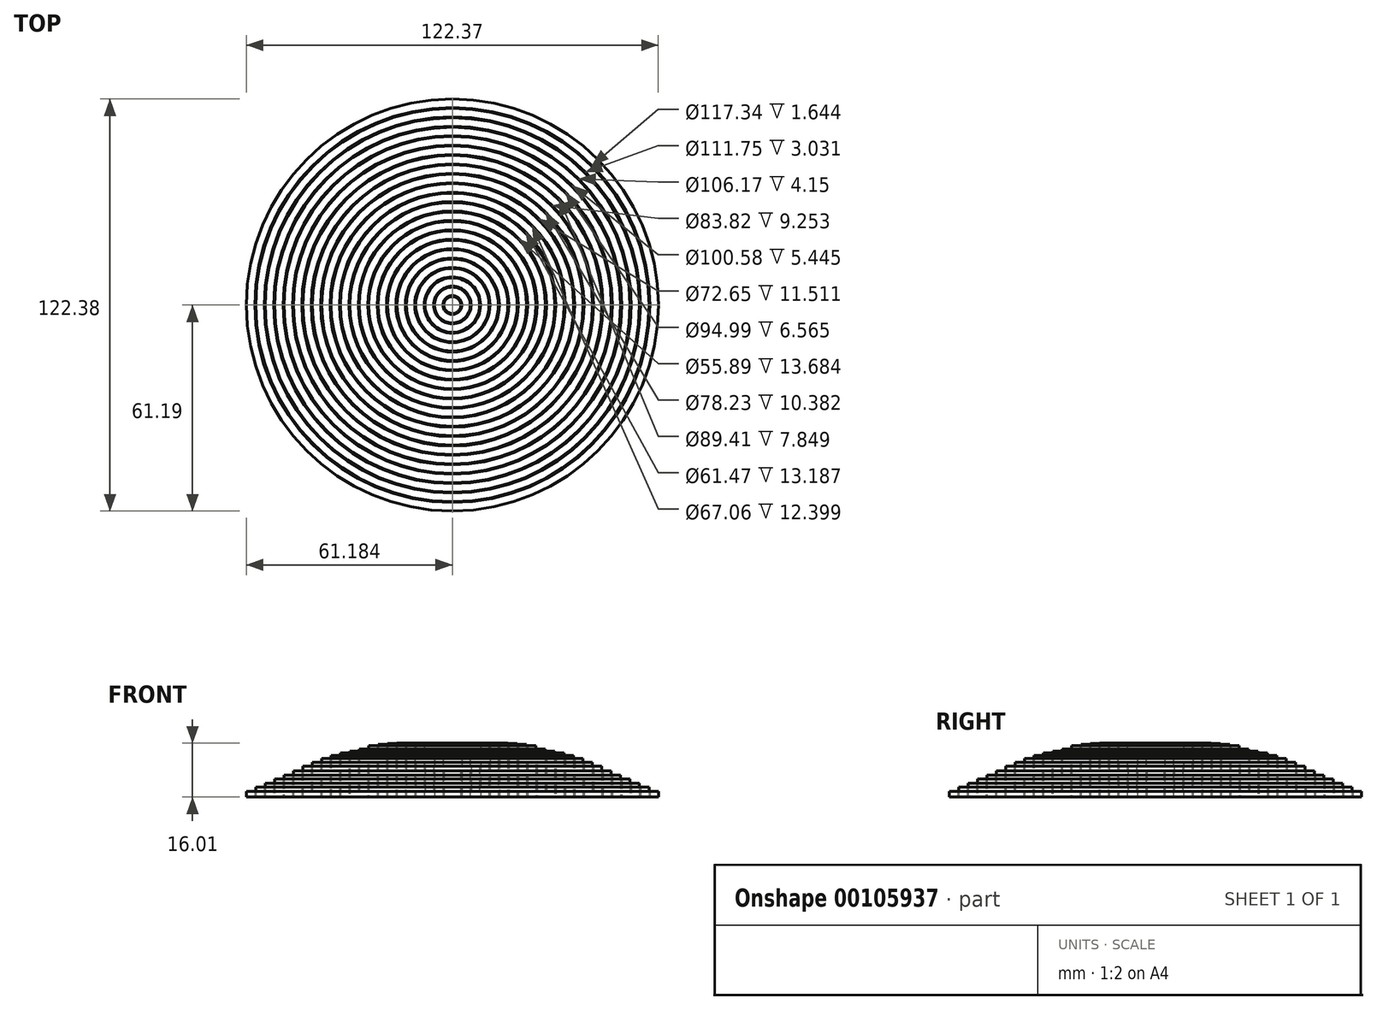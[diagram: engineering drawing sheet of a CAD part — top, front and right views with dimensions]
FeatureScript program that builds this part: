
annotation { "Feature Type Name" : "Feature", "Feature Type Description" : "" }
export const myFeature = defineFeature(function(context is Context, id is Id, definition is map)
    precondition{}
    {
        {
            var Q0;
            Q0=qCreatedBy(makeId("Front.planeOp"),FACE);
            var sketch = newSketch(context, id + "F0", { "sketchPlane" : qUnion([Q0])});
            skLineSegment(sketch, "E0", {"start": v(0, 7.88) * mm, "end": v(2.51, 7.88) * mm});
            skLineSegment(sketch, "E1", {"start": v(2.51, 7.88) * mm, "end": v(2.51, 0.01) * mm});
            skLineSegment(sketch, "E2", {"start": v(2.51, 0.01) * mm, "end": v(0, 0.01) * mm});
            skLineSegment(sketch, "E3", {"start": v(0, 0.01) * mm, "end": v(0, 7.88) * mm});
            skLineSegment(sketch, "E4", {"start": v(2.8, 11.92) * mm, "end": v(5.3, 11.92) * mm});
            skLineSegment(sketch, "E5", {"start": v(5.3, 11.92) * mm, "end": v(5.3, 0.01) * mm});
            skLineSegment(sketch, "E6", {"start": v(5.3, 0.01) * mm, "end": v(2.8, 0.01) * mm});
            skLineSegment(sketch, "E7", {"start": v(2.8, 0.01) * mm, "end": v(2.8, 11.92) * mm});
            skLineSegment(sketch, "E8", {"start": v(5.6, 14.05) * mm, "end": v(8.1, 14.05) * mm});
            skLineSegment(sketch, "E9", {"start": v(8.1, 14.05) * mm, "end": v(8.1, 0.01) * mm});
            skLineSegment(sketch, "E10", {"start": v(8.1, 0.01) * mm, "end": v(5.6, 0.01) * mm});
            skLineSegment(sketch, "E11", {"start": v(5.6, 0.01) * mm, "end": v(5.6, 14.05) * mm});
            skLineSegment(sketch, "E12", {"start": v(8.39, 15.15) * mm, "end": v(10.9, 15.15) * mm});
            skLineSegment(sketch, "E13", {"start": v(10.9, 15.15) * mm, "end": v(10.9, 0.01) * mm});
            skLineSegment(sketch, "E14", {"start": v(10.9, 0.01) * mm, "end": v(8.39, 0.01) * mm});
            skLineSegment(sketch, "E15", {"start": v(8.39, 0.01) * mm, "end": v(8.39, 15.15) * mm});
            skLineSegment(sketch, "E16", {"start": v(11.18, 15.76) * mm, "end": v(13.69, 15.76) * mm});
            skLineSegment(sketch, "E17", {"start": v(13.69, 15.76) * mm, "end": v(13.69, 0.01) * mm});
            skLineSegment(sketch, "E18", {"start": v(13.69, 0.01) * mm, "end": v(11.18, 0.01) * mm});
            skLineSegment(sketch, "E19", {"start": v(11.18, 0.01) * mm, "end": v(11.18, 15.76) * mm});
            skLineSegment(sketch, "E20", {"start": v(13.98, 16.02) * mm, "end": v(16.48, 16.02) * mm});
            skLineSegment(sketch, "E21", {"start": v(16.48, 16.02) * mm, "end": v(16.48, 0.01) * mm});
            skLineSegment(sketch, "E22", {"start": v(16.48, 0.01) * mm, "end": v(13.98, 0.01) * mm});
            skLineSegment(sketch, "E23", {"start": v(13.98, 0.01) * mm, "end": v(13.98, 16.02) * mm});
            skLineSegment(sketch, "E24", {"start": v(16.77, 16) * mm, "end": v(19.27, 16) * mm});
            skLineSegment(sketch, "E25", {"start": v(19.27, 16) * mm, "end": v(19.27, 0.01) * mm});
            skLineSegment(sketch, "E26", {"start": v(19.27, 0.01) * mm, "end": v(16.77, 0.01) * mm});
            skLineSegment(sketch, "E27", {"start": v(16.77, 0.01) * mm, "end": v(16.77, 16) * mm});
            skLineSegment(sketch, "E28", {"start": v(19.57, 15.64) * mm, "end": v(22.07, 15.64) * mm});
            skLineSegment(sketch, "E29", {"start": v(22.07, 15.64) * mm, "end": v(22.07, 0.01) * mm});
            skLineSegment(sketch, "E30", {"start": v(22.07, 0.01) * mm, "end": v(19.57, 0.01) * mm});
            skLineSegment(sketch, "E31", {"start": v(19.57, 0.01) * mm, "end": v(19.57, 15.64) * mm});
            skLineSegment(sketch, "E32", {"start": v(22.36, 15.26) * mm, "end": v(24.86, 15.26) * mm});
            skLineSegment(sketch, "E33", {"start": v(24.86, 15.26) * mm, "end": v(24.86, 0.01) * mm});
            skLineSegment(sketch, "E34", {"start": v(24.86, 0.01) * mm, "end": v(22.36, 0.01) * mm});
            skLineSegment(sketch, "E35", {"start": v(22.36, 0.01) * mm, "end": v(22.36, 15.26) * mm});
            skLineSegment(sketch, "E36", {"start": v(25.15, 14.32) * mm, "end": v(27.66, 14.32) * mm});
            skLineSegment(sketch, "E37", {"start": v(27.66, 14.32) * mm, "end": v(27.66, 0.01) * mm});
            skLineSegment(sketch, "E38", {"start": v(27.66, 0.01) * mm, "end": v(25.15, 0.01) * mm});
            skLineSegment(sketch, "E39", {"start": v(25.15, 0.01) * mm, "end": v(25.15, 14.32) * mm});
            skLineSegment(sketch, "E40", {"start": v(27.95, 13.7) * mm, "end": v(30.45, 13.7) * mm});
            skLineSegment(sketch, "E41", {"start": v(30.45, 13.7) * mm, "end": v(30.45, 0.01) * mm});
            skLineSegment(sketch, "E42", {"start": v(30.45, 0.01) * mm, "end": v(27.95, 0.01) * mm});
            skLineSegment(sketch, "E43", {"start": v(27.95, 0.01) * mm, "end": v(27.95, 13.7) * mm});
            skLineSegment(sketch, "E44", {"start": v(30.74, 13.2) * mm, "end": v(33.24, 13.2) * mm});
            skLineSegment(sketch, "E45", {"start": v(33.24, 13.2) * mm, "end": v(33.24, 0.01) * mm});
            skLineSegment(sketch, "E46", {"start": v(33.24, 0.01) * mm, "end": v(30.74, 0.01) * mm});
            skLineSegment(sketch, "E47", {"start": v(30.74, 0.01) * mm, "end": v(30.74, 13.2) * mm});
            skLineSegment(sketch, "E48", {"start": v(33.53, 12.41) * mm, "end": v(36.04, 12.41) * mm});
            skLineSegment(sketch, "E49", {"start": v(36.04, 12.41) * mm, "end": v(36.04, 0.01) * mm});
            skLineSegment(sketch, "E50", {"start": v(36.04, 0.01) * mm, "end": v(33.53, 0.01) * mm});
            skLineSegment(sketch, "E51", {"start": v(33.53, 0.01) * mm, "end": v(33.53, 12.41) * mm});
            skLineSegment(sketch, "E52", {"start": v(36.33, 11.52) * mm, "end": v(38.83, 11.52) * mm});
            skLineSegment(sketch, "E53", {"start": v(38.83, 11.52) * mm, "end": v(38.83, 0.01) * mm});
            skLineSegment(sketch, "E54", {"start": v(38.83, 0.01) * mm, "end": v(36.33, 0.01) * mm});
            skLineSegment(sketch, "E55", {"start": v(36.33, 0.01) * mm, "end": v(36.33, 11.52) * mm});
            skLineSegment(sketch, "E56", {"start": v(39.12, 10.4) * mm, "end": v(41.63, 10.4) * mm});
            skLineSegment(sketch, "E57", {"start": v(41.63, 10.4) * mm, "end": v(41.63, 0.01) * mm});
            skLineSegment(sketch, "E58", {"start": v(41.63, 0.01) * mm, "end": v(39.12, 0.01) * mm});
            skLineSegment(sketch, "E59", {"start": v(39.12, 0.01) * mm, "end": v(39.12, 10.4) * mm});
            skLineSegment(sketch, "E60", {"start": v(41.91, 9.27) * mm, "end": v(44.42, 9.27) * mm});
            skLineSegment(sketch, "E61", {"start": v(44.42, 9.27) * mm, "end": v(44.42, 0.01) * mm});
            skLineSegment(sketch, "E62", {"start": v(44.42, 0.01) * mm, "end": v(41.91, 0.01) * mm});
            skLineSegment(sketch, "E63", {"start": v(41.91, 0.01) * mm, "end": v(41.91, 9.27) * mm});
            skLineSegment(sketch, "E64", {"start": v(44.7, 7.86) * mm, "end": v(47.22, 7.86) * mm});
            skLineSegment(sketch, "E65", {"start": v(47.22, 7.86) * mm, "end": v(47.22, 0.01) * mm});
            skLineSegment(sketch, "E66", {"start": v(47.22, 0.01) * mm, "end": v(44.7, 0.01) * mm});
            skLineSegment(sketch, "E67", {"start": v(44.7, 0.01) * mm, "end": v(44.7, 7.86) * mm});
            skLineSegment(sketch, "E68", {"start": v(47.5, 6.58) * mm, "end": v(50.01, 6.58) * mm});
            skLineSegment(sketch, "E69", {"start": v(50.01, 6.58) * mm, "end": v(50.01, 0.01) * mm});
            skLineSegment(sketch, "E70", {"start": v(50.01, 0.01) * mm, "end": v(47.5, 0.01) * mm});
            skLineSegment(sketch, "E71", {"start": v(47.5, 0.01) * mm, "end": v(47.5, 6.58) * mm});
            skLineSegment(sketch, "E72", {"start": v(50.3, 5.46) * mm, "end": v(52.8, 5.46) * mm});
            skLineSegment(sketch, "E73", {"start": v(52.8, 5.46) * mm, "end": v(52.8, 0.01) * mm});
            skLineSegment(sketch, "E74", {"start": v(52.8, 0.01) * mm, "end": v(50.3, 0.01) * mm});
            skLineSegment(sketch, "E75", {"start": v(50.3, 0.01) * mm, "end": v(50.3, 5.46) * mm});
            skLineSegment(sketch, "E76", {"start": v(53.09, 4.16) * mm, "end": v(55.6, 4.16) * mm});
            skLineSegment(sketch, "E77", {"start": v(55.6, 4.16) * mm, "end": v(55.6, 0.01) * mm});
            skLineSegment(sketch, "E78", {"start": v(55.6, 0.01) * mm, "end": v(53.09, 0.01) * mm});
            skLineSegment(sketch, "E79", {"start": v(53.09, 0.01) * mm, "end": v(53.09, 4.16) * mm});
            skLineSegment(sketch, "E80", {"start": v(55.88, 3.04) * mm, "end": v(58.4, 3.04) * mm});
            skLineSegment(sketch, "E81", {"start": v(58.4, 3.04) * mm, "end": v(58.4, 0.01) * mm});
            skLineSegment(sketch, "E82", {"start": v(58.4, 0.01) * mm, "end": v(55.88, 0.01) * mm});
            skLineSegment(sketch, "E83", {"start": v(55.88, 0.01) * mm, "end": v(55.88, 3.04) * mm});
            skLineSegment(sketch, "E84", {"start": v(58.67, 1.66) * mm, "end": v(61.2, 1.66) * mm});
            skLineSegment(sketch, "E85", {"start": v(61.2, 1.66) * mm, "end": v(61.2, 0.01) * mm});
            skLineSegment(sketch, "E86", {"start": v(61.2, 0.01) * mm, "end": v(58.67, 0.01) * mm});
            skLineSegment(sketch, "E87", {"start": v(58.67, 0.01) * mm, "end": v(58.67, 1.66) * mm});
            skLineSegment(sketch, "E88", {"start": v(0, 0.01) * mm, "end": v(0, 29.32) * mm});
            skSolve(sketch);
        }
        {
            var Q0;
            {var subQ0=sQuery(id+"F0.wireOp",EDGE,"E0");Q0=makeQuery(id+"F0.imprint","IMPRINT",FACE,{"disambiguationData":[TD([[makeQuery(id+"F0.imprint","IMPRINT",EDGE,{"derivedFrom":subQ0}),-1.0]])]});}
            var Q1;
            Q1=makeQuery(id+"F0.imprint","IMPRINT",FACE,{"disambiguationData":[TD([[makeQuery(id+"F0.imprint","IMPRINT",EDGE,{"derivedFrom":sQuery(id+"F0.wireOp",EDGE,"E4")}),-1.0]])]});
            var Q2;
            Q2=makeQuery(id+"F0.imprint","IMPRINT",FACE,{"disambiguationData":[TD([[makeQuery(id+"F0.imprint","IMPRINT",EDGE,{"derivedFrom":sQuery(id+"F0.wireOp",EDGE,"E8")}),-1.0]])]});
            var Q3;
            Q3=makeQuery(id+"F0.imprint","IMPRINT",FACE,{"disambiguationData":[TD([[makeQuery(id+"F0.imprint","IMPRINT",EDGE,{"derivedFrom":sQuery(id+"F0.wireOp",EDGE,"E12")}),-1.0]])]});
            var Q4;
            Q4=makeQuery(id+"F0.imprint","IMPRINT",FACE,{"disambiguationData":[TD([[makeQuery(id+"F0.imprint","IMPRINT",EDGE,{"derivedFrom":sQuery(id+"F0.wireOp",EDGE,"E16")}),-1.0]])]});
            var Q5;
            Q5=makeQuery(id+"F0.imprint","IMPRINT",FACE,{"disambiguationData":[TD([[makeQuery(id+"F0.imprint","IMPRINT",EDGE,{"derivedFrom":sQuery(id+"F0.wireOp",EDGE,"E20")}),-1.0]])]});
            var Q6;
            Q6=makeQuery(id+"F0.imprint","IMPRINT",FACE,{"disambiguationData":[TD([[makeQuery(id+"F0.imprint","IMPRINT",EDGE,{"derivedFrom":sQuery(id+"F0.wireOp",EDGE,"E24")}),-1.0]])]});
            var Q7;
            Q7=makeQuery(id+"F0.imprint","IMPRINT",FACE,{"disambiguationData":[TD([[makeQuery(id+"F0.imprint","IMPRINT",EDGE,{"derivedFrom":sQuery(id+"F0.wireOp",EDGE,"E28")}),-1.0]])]});
            var Q8;
            Q8=makeQuery(id+"F0.imprint","IMPRINT",FACE,{"disambiguationData":[TD([[makeQuery(id+"F0.imprint","IMPRINT",EDGE,{"derivedFrom":sQuery(id+"F0.wireOp",EDGE,"E32")}),-1.0]])]});
            var Q9;
            Q9=makeQuery(id+"F0.imprint","IMPRINT",FACE,{"disambiguationData":[TD([[makeQuery(id+"F0.imprint","IMPRINT",EDGE,{"derivedFrom":sQuery(id+"F0.wireOp",EDGE,"E36")}),-1.0]])]});
            var Q10;
            Q10=makeQuery(id+"F0.imprint","IMPRINT",FACE,{"disambiguationData":[TD([[makeQuery(id+"F0.imprint","IMPRINT",EDGE,{"derivedFrom":sQuery(id+"F0.wireOp",EDGE,"E40")}),-1.0]])]});
            var Q11;
            Q11=makeQuery(id+"F0.imprint","IMPRINT",FACE,{"disambiguationData":[TD([[makeQuery(id+"F0.imprint","IMPRINT",EDGE,{"derivedFrom":sQuery(id+"F0.wireOp",EDGE,"E44")}),-1.0]])]});
            var Q12;
            Q12=makeQuery(id+"F0.imprint","IMPRINT",FACE,{"disambiguationData":[TD([[makeQuery(id+"F0.imprint","IMPRINT",EDGE,{"derivedFrom":sQuery(id+"F0.wireOp",EDGE,"E48")}),-1.0]])]});
            var Q13;
            Q13=makeQuery(id+"F0.imprint","IMPRINT",FACE,{"disambiguationData":[TD([[makeQuery(id+"F0.imprint","IMPRINT",EDGE,{"derivedFrom":sQuery(id+"F0.wireOp",EDGE,"E52")}),-1.0]])]});
            var Q14;
            Q14=makeQuery(id+"F0.imprint","IMPRINT",FACE,{"disambiguationData":[TD([[makeQuery(id+"F0.imprint","IMPRINT",EDGE,{"derivedFrom":sQuery(id+"F0.wireOp",EDGE,"E56")}),-1.0]])]});
            var Q15;
            Q15=makeQuery(id+"F0.imprint","IMPRINT",FACE,{"disambiguationData":[TD([[makeQuery(id+"F0.imprint","IMPRINT",EDGE,{"derivedFrom":sQuery(id+"F0.wireOp",EDGE,"E60")}),-1.0]])]});
            var Q16;
            Q16=makeQuery(id+"F0.imprint","IMPRINT",FACE,{"disambiguationData":[TD([[makeQuery(id+"F0.imprint","IMPRINT",EDGE,{"derivedFrom":sQuery(id+"F0.wireOp",EDGE,"E64")}),-1.0]])]});
            var Q17;
            Q17=makeQuery(id+"F0.imprint","IMPRINT",FACE,{"disambiguationData":[TD([[makeQuery(id+"F0.imprint","IMPRINT",EDGE,{"derivedFrom":sQuery(id+"F0.wireOp",EDGE,"E68")}),-1.0]])]});
            var Q18;
            Q18=makeQuery(id+"F0.imprint","IMPRINT",FACE,{"disambiguationData":[TD([[makeQuery(id+"F0.imprint","IMPRINT",EDGE,{"derivedFrom":sQuery(id+"F0.wireOp",EDGE,"E72")}),-1.0]])]});
            var Q19;
            Q19=makeQuery(id+"F0.imprint","IMPRINT",FACE,{"disambiguationData":[TD([[makeQuery(id+"F0.imprint","IMPRINT",EDGE,{"derivedFrom":sQuery(id+"F0.wireOp",EDGE,"E76")}),-1.0]])]});
            var Q20;
            Q20=makeQuery(id+"F0.imprint","IMPRINT",FACE,{"disambiguationData":[TD([[makeQuery(id+"F0.imprint","IMPRINT",EDGE,{"derivedFrom":sQuery(id+"F0.wireOp",EDGE,"E80")}),-1.0]])]});
            var Q21;
            Q21=makeQuery(id+"F0.imprint","IMPRINT",FACE,{"disambiguationData":[TD([[makeQuery(id+"F0.imprint","IMPRINT",EDGE,{"derivedFrom":sQuery(id+"F0.wireOp",EDGE,"E84")}),-1.0]])]});
            var Q22;
            Q22=sQuery(id+"F0.wireOp",EDGE,"E88");
            revolve(context, id + "F1", {"entities" : qUnion([Q0, Q1, Q2, Q3, Q4, Q5, Q6, Q7, Q8, Q9, Q10, Q11, Q12, Q13, Q14, Q15, Q16, Q17, Q18, Q19, Q20, Q21]), "axis" : qUnion([Q22]), "revolveType" : RevolveType.FULL});
        }
    });
